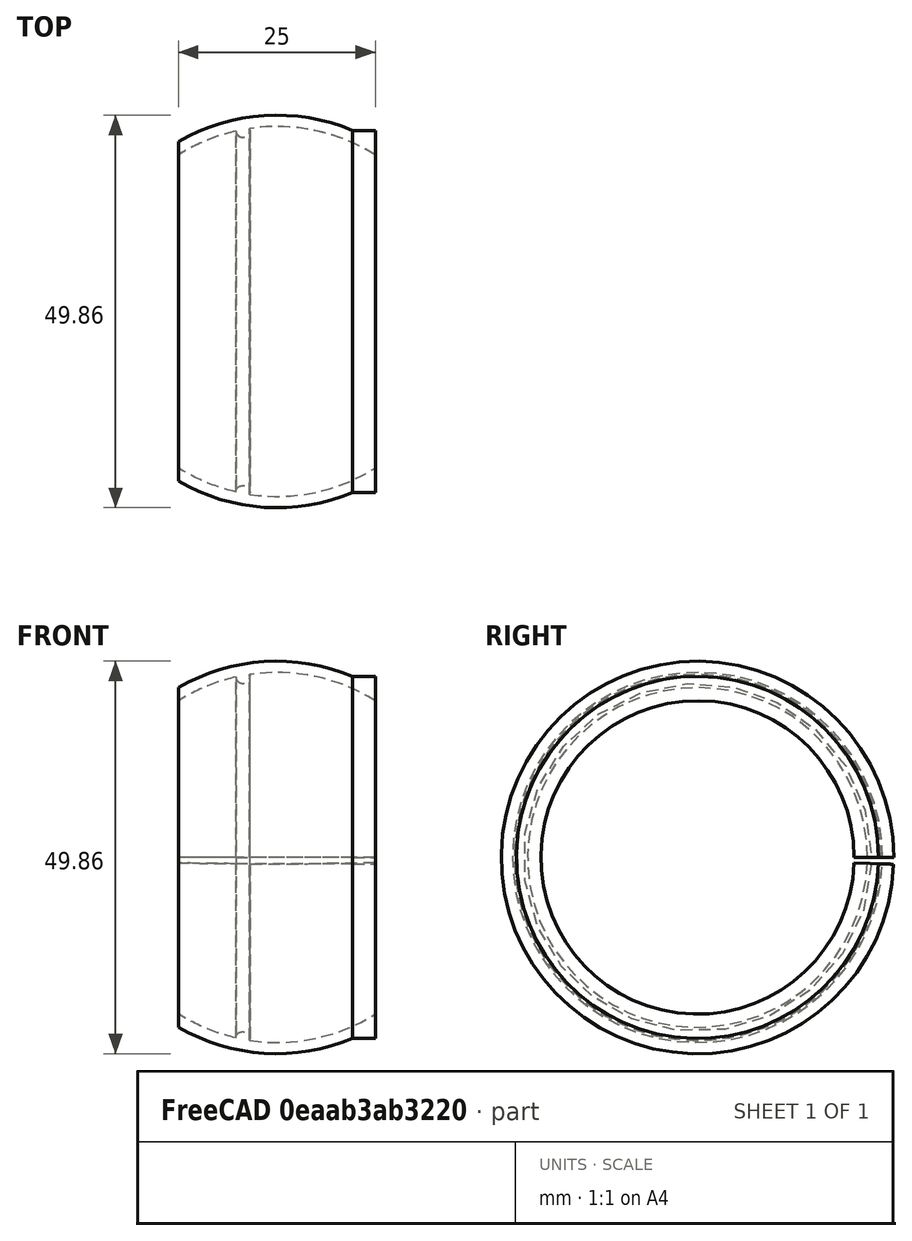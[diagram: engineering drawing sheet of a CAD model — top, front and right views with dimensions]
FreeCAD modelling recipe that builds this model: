
FCSTD DOCUMENT  (FreeCAD 0.18R16110 (Git))
Label: bearinghubbague
License: All rights reserved
LicenseURL: http://en.wikipedia.org/wiki/All_rights_reserved
objects: Mesh::Feature×3, Sketcher::SketchObject×1, Part::Revolution×1
note: 2 computed .brp shape members not serialized (recipe doc carries the construction recipe); baked Part::Feature solids carry a one-line shape summary decoded from their .brp

FEATURE [Sketcher::SketchObject] Sketch
  sketch-geometry (11):
    g0: ArcOfCircle CenterX=0 CenterY=0 CenterZ=0 NormalX=0 NormalY=0 NormalZ=1 AngleXU=0 Radius=23.5 StartAngle=1.00994 EndAngle=1.71812
    g1: ArcOfCircle CenterX=0 CenterY=0 CenterZ=0 NormalX=0 NormalY=0 NormalZ=1 AngleXU=0 Radius=24.9328 StartAngle=1.17446 EndAngle=2.09595
    g2: LineSegment StartX=12.5 StartY=21.8998 StartZ=0 EndX=12.5 EndY=19.8997 EndZ=0
    g3: LineSegment StartX=-12.5 StartY=21.573 StartZ=0 EndX=-12.5 EndY=19.8997 EndZ=0
    g4: LineSegment [constr] StartX=-12.5 StartY=19.8997 StartZ=0 EndX=12.5 EndY=19.8997 EndZ=0
    g5: GeomPoint X=-7.36008 Y=22.3177 Z=0
    g6: GeomPoint X=-7.3108 Y=22.8515 Z=0
    g7: ArcOfCircle CenterX=-4.32144 CenterY=23.0217 CenterZ=0 NormalX=0 NormalY=0 NormalZ=1 AngleXU=0 Radius=0.9 StartAngle=3.26154 EndAngle=6.53441
    g8: ArcOfCircle CenterX=-0.000204642 CenterY=9.13448e-05 CenterZ=0 NormalX=0 NormalY=0 NormalZ=1 AngleXU=0 Radius=23.4998 StartAngle=1.79457 EndAngle=2.13165
    g9: LineSegment StartX=9.62509 StartY=23 StartZ=0 EndX=12.5 EndY=23 EndZ=0
    g10: LineSegment StartX=12.5 StartY=23 StartZ=0 EndX=12.5 EndY=21.8998 EndZ=0
  constraints (22):
    c: Coincident(g0,g-1)
    c: Coincident(g1,g0)
    c: Coincident(g2,g0)
    c: Vertical(g2)
    c: Coincident(g3,g1)
    c: Coincident(g3,g8)
    c: Vertical(g3)
    c: Symmetric(g0,g8,g-2)
    c: Coincident(g4,g8)
    c: Coincident(g4,g0)
    c: Radius(g0) = 23.5
    c: DistanceX(g4,g4) = 25
    c: PointOnObject(g5,g0)
    c: Radius(g7) = 0.9
    c: Coincident(g7,g0)
    c: Coincident(g8,g7)
    c: Coincident(g9,g10)
    c: Coincident(g10,g2)
    c: Coincident(g1,g9)
    c: Vertical(g10)
    c: Angle(g9,g10) = 1.5708
    c: DistanceY(g9) = 23
FEATURE [Part::Revolution] Revolve
  Angle = 358
  Axis = (1,0,0)
  Base = (0,0,0)
  FaceMakerClass = Part::FaceMakerBullseye
  Solid = true
  Source = -> Sketch
  Symmetric = false
FEATURE [Mesh::Feature] leg
  Placement = pos=(19.76,-21,0) rot=(0,1,0;-1.5708rad)
FEATURE [Mesh::Feature] handle
  Placement = pos=(-1,31,0) rot=(1,0,0;6.26573rad)
FEATURE [Mesh::Feature] handle001
  Placement = pos=(-1,31,-2.9) rot=(-1,0,0;6.26573rad)
